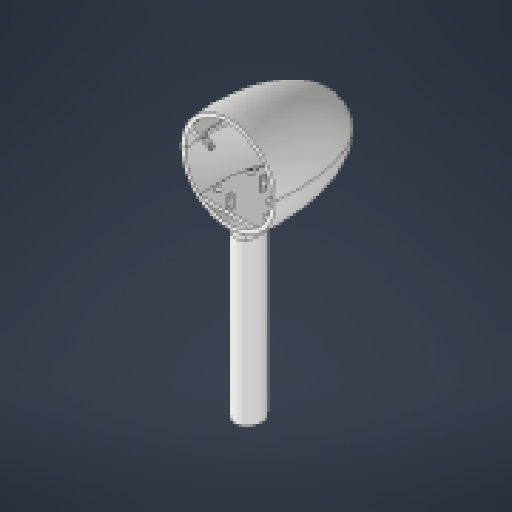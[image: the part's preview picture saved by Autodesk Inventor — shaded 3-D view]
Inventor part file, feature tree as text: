
AUTODESK INVENTOR PART (.ipt)
format: ipt  version: 2023.2 (Build 272271000, 271)  size: 766,464 bytes
history: native  units: mm
features: extrude x10, other x7, sketch x7, revolve x2, shell x2, mirror x2, pattern_circular x1, fillet x1
ambient origin geometry x8: Origin, YZ Plane, XZ Plane, XY Plane, X Axis, Y Axis, Z Axis, Center Point
bodies: Body1 (feature_tree), Body2 (feature_tree), Body3 (feature_tree)
feature tree (32):
  other  "Gehäuse unten"
  sketch  "Skizze1"  dims[d3=160.0mm d29=180.0deg d30=6.0mm]
  revolve  "Umdrehung3"
  shell  "Wandung4"  Thickness=80.0mm
  extrude  "Extrusion4"  TaperAngle=180.0deg  [1 undecoded]
  mirror  "Spiegeln1"
  revolve  "Umdrehung4"
  shell  "Wandung5"  Thickness=6.0mm
  extrude  "Extrusion5"  Depth=3.1mm
  mirror  "Spiegeln2"
  other  "Körper verschieben3"
  extrude  "Extrusion6"  Depth=3.1mm
  extrude  "Extrusion7"  Depth=3.1mm
  extrude  "Extrusion8"  Depth=10.0mm
  extrude  "Extrusion9"  Depth=3.1mm
  extrude  "Extrusion11"  Depth=3.1mm
  other  "Arbeitsachse1"
  pattern_circular  "Runde Anordnung1"  [2 undecoded]
  extrude  "Extrusion12"  Depth=3.1mm
  extrude  "Extrusion13"  Depth=3.1mm
  extrude  "Extrusion14"  Depth=3.1mm
  other  "Kombinieren1"
  fillet  "Rundung2"  Radius=3.1mm
  other  "Gehäuse oben"
  sketch  "Skizze17"  dims[d31=3.0mm d32=3.1mm]
  other  "Turm"
  sketch  "Skizze18"  dims[d33=5.0mm d34=3.1mm]
  sketch  "Skizze26"  dims[d35=3.1mm d37=3.1mm]
  sketch  "Skizze27"  dims[d38=10.0mm d39=10.0mm]
  sketch  "Skizze28"  dims[d40=10.0mm d41=3.1mm]
  sketch  "Skizze29"  dims[d42=3.1mm d43=3.1mm d44=3.1mm d45=3.1mm d46=3.1mm d47=3.1mm d48=3.1mm d49=3.1mm d50=3.1mm d51=10.0mm d52=10.0mm d53=10.0mm d54=10.0mm d55=10.0mm d56=10.0mm d57=10.0mm d58=10.0mm d59=10.0mm d61=3.1mm d62=3.1mm d63=10.0mm d64=10.0mm d65=10.0mm d66=3.1mm d67=3.1mm d68=0.0mm d69=180.0deg d70=6.0mm d71=3.1mm d72=0.0mm d73=0.0mm d74=0.0001mm d75=0.0mm d82=5.0mm d83=50.0mm d84=85.0mm d85=10.0mm d86=0.0mm d87=39.0mm d88=250.0mm d89=0.0mm d90=5.7mm d91=0.0mm d92=0.0mm d93=30.0deg d94=120.0deg d96=55.0mm d97=2.5mm d98=31.0mm d100=18.0mm d102=2.0mm d103=20.0mm d105=120.0deg d107=54.0mm d108=0.0mm d113=20.0mm d114=40.0mm d115=7.0mm d116=7.0mm d117=0.0mm d118=20.0mm d119=120.0deg d121=4.0mm d122=4.0mm d123=4.0mm d124=20.0mm d126=48.0mm d127=20.0mm d129=10.0mm d132=50.0mm d133=0.5mm d134=2.5mm d136=54.0mm d137=0.0mm d138=40.0mm d139=19.0mm d140=7.0mm d141=4.0mm d142=4.0mm d143=4.0mm d144=20.0mm d146=48.0mm d147=20.0mm d149=10.0mm d152=10.0mm d153=0.0mm d154=8.0mm d155=20.0mm d156=35.0mm d157=7.0mm d158=0.0mm d159=8.0mm d160=13.0mm d161=62.2mm d162=15.0mm d163=45.0mm d164=20.0mm d165=19.0mm d166=30.0mm d167=90.0deg d168=23.911011mm d169=23.212879mm d170=40.5mm d172=69.0mm d175=90.0deg d177=140.0mm d178=38.0mm d179=90.0deg d180=77.358929mm d181=25.00527mm d182=20.0mm]
  other  "Platte"
note: 3 required parameter values undecoded (feature->parameter linkage not recoverable at this tier; creation-order binding heuristic only, values carry confidence <= 0.55)
